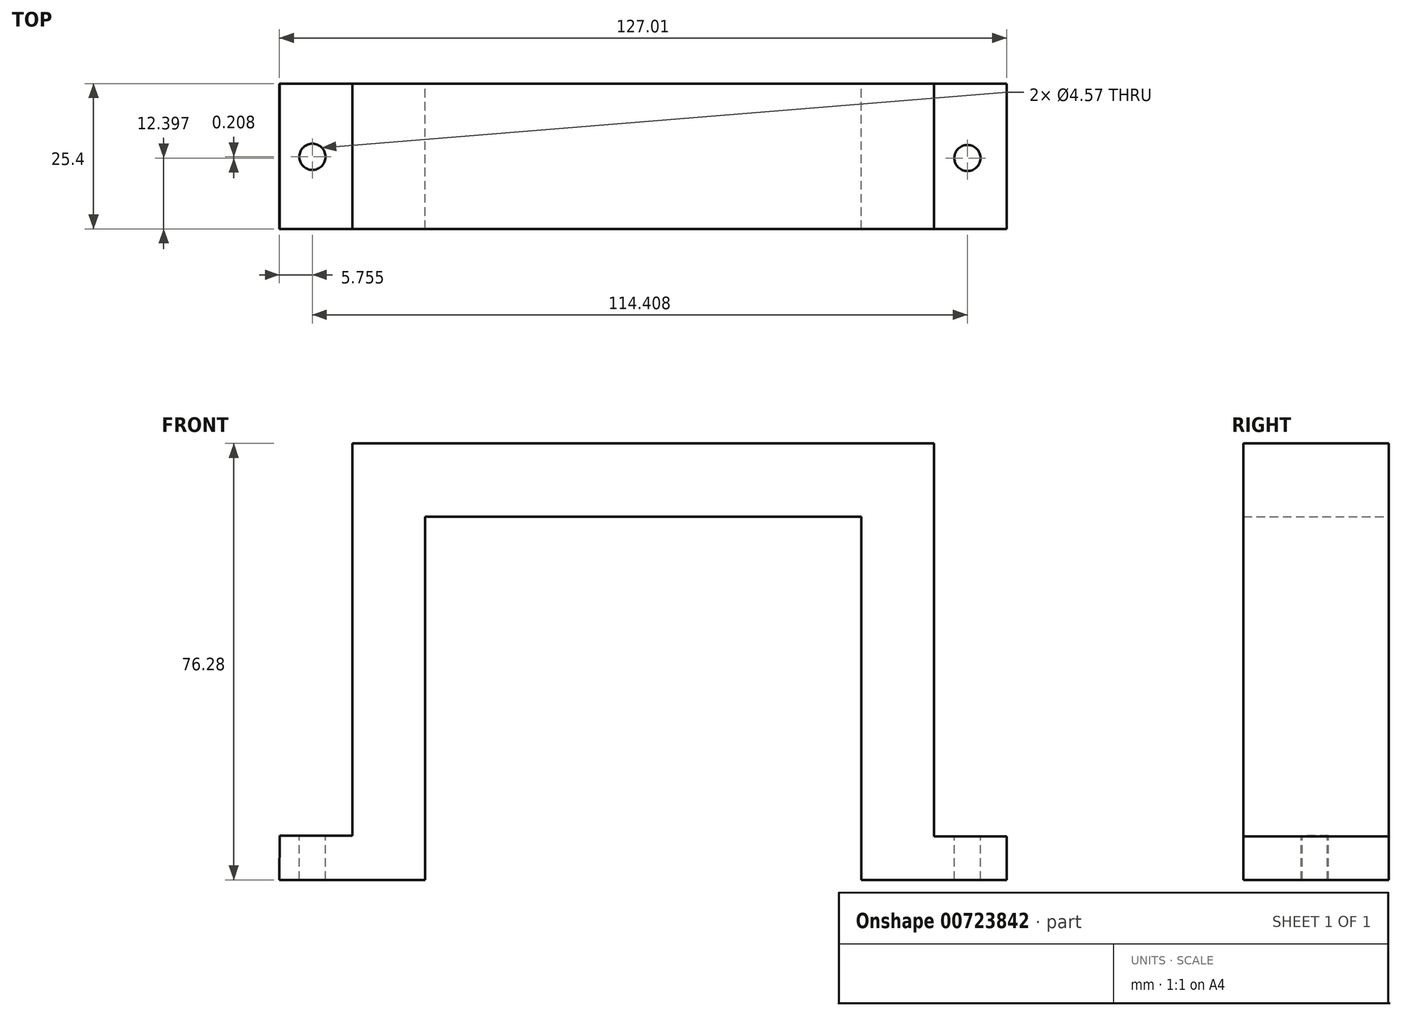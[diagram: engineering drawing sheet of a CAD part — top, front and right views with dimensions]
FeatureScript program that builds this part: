
annotation { "Feature Type Name" : "Feature", "Feature Type Description" : "" }
export const myFeature = defineFeature(function(context is Context, id is Id, definition is map)
    precondition{}
    {
        {
            var Q0;
            Q0=qCreatedBy(makeId("Front.planeOp"),FACE);
            var sketch = newSketch(context, id + "F0", { "sketchPlane" : qUnion([Q0])});
            skLineSegment(sketch, "E0", {"start": v(-45.35, -75.77) * mm, "end": v(-58.05, -75.77) * mm});
            skLineSegment(sketch, "E1", {"start": v(-45.35, -75.77) * mm, "end": v(-45.35, -7.2) * mm});
            skLineSegment(sketch, "E2", {"start": v(-45.35, -7.2) * mm, "end": v(56.25, -7.2) * mm});
            skLineSegment(sketch, "E3", {"start": v(56.25, -7.2) * mm, "end": v(56.25, -75.85) * mm});
            skLineSegment(sketch, "E4", {"start": v(56.25, -75.85) * mm, "end": v(68.95, -75.85) * mm});
            skLineSegment(sketch, "E5", {"start": v(68.95, -75.85) * mm, "end": v(68.95, -83.47) * mm});
            skLineSegment(sketch, "E6", {"start": v(68.95, -83.47) * mm, "end": v(43.55, -83.47) * mm});
            skLineSegment(sketch, "E7", {"start": v(43.55, -83.47) * mm, "end": v(43.55, -19.97) * mm});
            skLineSegment(sketch, "E8", {"start": v(43.55, -19.97) * mm, "end": v(-32.65, -19.97) * mm});
            skLineSegment(sketch, "E9", {"start": v(-32.65, -19.97) * mm, "end": v(-32.65, -83.47) * mm});
            skLineSegment(sketch, "E10", {"start": v(-32.65, -83.47) * mm, "end": v(-58.06, -83.47) * mm});
            skLineSegment(sketch, "E11", {"start": v(-58.06, -83.47) * mm, "end": v(-58.05, -75.77) * mm});
            skSolve(sketch);
        }
        {
            var Q0;
            Q0=makeQuery(id+"F0.imprint","IMPRINT",FACE,{"disambiguationData":[TD([[makeQuery(id+"F0.imprint","IMPRINT",EDGE,{"derivedFrom":sQuery(id+"F0.wireOp",EDGE,"E0")}),1.0]])]});
            extrude(context, id + "F1", {"entities" : qUnion([Q0]), "depth" : 25.4 * mm, "offsetDistance" : 25.4 * mm});
        }
        {
            var Q0;
            Q0=qCreatedBy(makeId("Top.planeOp"),FACE);
            var sketch = newSketch(context, id + "F2", { "sketchPlane" : qUnion([Q0])});
            skCircle(sketch, "E12", {"center": v(-52.3, -12.8) * mm, "radius": 2.29 * mm});
            skSolve(sketch);
        }
        {
            var Q0;
            Q0=sQuery(id+"F2.wireOp",VERTEX,"E12.center");
            var Q1;
            Q1=makeQuery(id+"F1.opExtrude","SWEPT_BODY",BODY,{"disambiguationData":[OSD([sQuery(id+"F0.wireOp",EDGE,"E0"),sQuery(id+"F0.wireOp",EDGE,"E1"),sQuery(id+"F0.wireOp",EDGE,"E2"),sQuery(id+"F0.wireOp",EDGE,"E3"),sQuery(id+"F0.wireOp",EDGE,"E4"),sQuery(id+"F0.wireOp",EDGE,"E5"),sQuery(id+"F0.wireOp",EDGE,"E6"),sQuery(id+"F0.wireOp",EDGE,"E7"),sQuery(id+"F0.wireOp",EDGE,"E8"),sQuery(id+"F0.wireOp",EDGE,"E9"),sQuery(id+"F0.wireOp",EDGE,"E10"),sQuery(id+"F0.wireOp",EDGE,"E11")])]});
            hole(context, id + "F3", {"style" : HoleStyle.SIMPLE, "endStyle" : HoleEndStyle.THROUGH, "holeDiameter" : 4.57 * mm, "majorDiameter" : 6.35 * mm, "isTappedThrough" : true, "tappedDepth" : 12.7 * mm, "tapClearance" : 3, "locations" : qUnion([Q0]), "scope" : qUnion([Q1])});
        }
        {
            var Q0;
            Q0=qCreatedBy(makeId("Top.planeOp"),FACE);
            var sketch = newSketch(context, id + "F4", { "sketchPlane" : qUnion([Q0])});
            skCircle(sketch, "E13", {"center": v(62.1, -13) * mm, "radius": 2.29 * mm});
            skSolve(sketch);
        }
        {
            var Q0;
            Q0=sQuery(id+"F4.wireOp",VERTEX,"E13.center");
            var Q1;
            Q1=makeQuery(id+"F1.opExtrude","SWEPT_BODY",BODY,{"disambiguationData":[OSD([sQuery(id+"F0.wireOp",EDGE,"E0"),sQuery(id+"F0.wireOp",EDGE,"E1"),sQuery(id+"F0.wireOp",EDGE,"E2"),sQuery(id+"F0.wireOp",EDGE,"E3"),sQuery(id+"F0.wireOp",EDGE,"E4"),sQuery(id+"F0.wireOp",EDGE,"E5"),sQuery(id+"F0.wireOp",EDGE,"E6"),sQuery(id+"F0.wireOp",EDGE,"E7"),sQuery(id+"F0.wireOp",EDGE,"E8"),sQuery(id+"F0.wireOp",EDGE,"E9"),sQuery(id+"F0.wireOp",EDGE,"E10"),sQuery(id+"F0.wireOp",EDGE,"E11")])]});
            hole(context, id + "F5", {"style" : HoleStyle.SIMPLE, "endStyle" : HoleEndStyle.THROUGH, "holeDiameter" : 4.57 * mm, "majorDiameter" : 6.35 * mm, "isTappedThrough" : true, "tappedDepth" : 12.7 * mm, "tapClearance" : 3, "locations" : qUnion([Q0]), "scope" : qUnion([Q1])});
        }
    });
